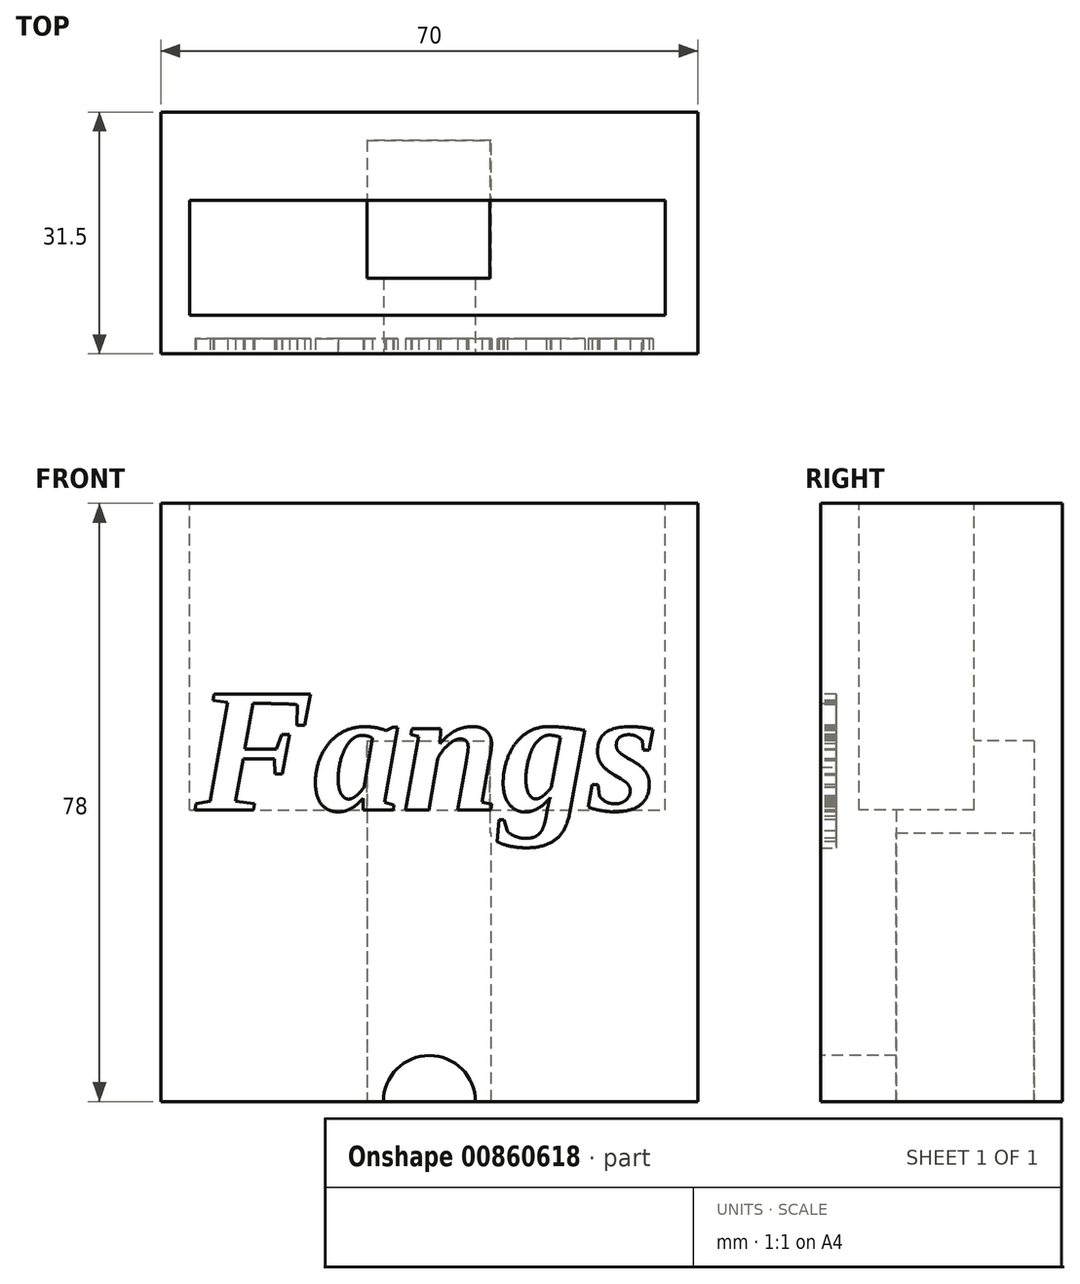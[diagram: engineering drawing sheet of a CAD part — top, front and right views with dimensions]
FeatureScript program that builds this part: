
annotation { "Feature Type Name" : "Feature", "Feature Type Description" : "" }
export const myFeature = defineFeature(function(context is Context, id is Id, definition is map)
    precondition{}
    {
        {
            var Q0;
            Q0=qCreatedBy(makeId("Front.planeOp"),FACE);
            var sketch = newSketch(context, id + "F0", { "sketchPlane" : qUnion([Q0])});
            skLineSegment(sketch, "E0", {"start": v(0, 0) * mm, "end": v(70, 0) * mm});
            skLineSegment(sketch, "E1", {"start": v(70, 0) * mm, "end": v(70, 40) * mm});
            skLineSegment(sketch, "E2", {"start": v(70, 40) * mm, "end": v(0, 40) * mm});
            skLineSegment(sketch, "E3", {"start": v(0, 40) * mm, "end": v(0, 0) * mm});
            skSolve(sketch);
        }
        {
            var Q0;
            Q0 = qSketchRegion(id + "F0", true);
            extrude(context, id + "F1", {"entities" : qUnion([Q0]), "depth" : 23 * mm, "offsetDistance" : 25 * mm});
        }
        {
            var Q0;
            Q0=makeQuery(id+"F1.opExtrude","CAP_FACE",FACE,{"disambiguationData":[OSD([sQuery(id+"F0.wireOp",EDGE,"E0"),sQuery(id+"F0.wireOp",EDGE,"E1"),sQuery(id+"F0.wireOp",EDGE,"E2"),sQuery(id+"F0.wireOp",EDGE,"E3")])],"isStart":false});
            var sketch = newSketch(context, id + "F2", { "sketchPlane" : qUnion([Q0])});
            skLineSegment(sketch, "E4.bottom", {"start": v(3.74, 0) * mm, "end": v(65.74, 0) * mm});
            skLineSegment(sketch, "E4.top", {"start": v(3.74, 40) * mm, "end": v(65.74, 40) * mm});
            skLineSegment(sketch, "E4.left", {"start": v(3.74, 0) * mm, "end": v(3.74, 40) * mm});
            skLineSegment(sketch, "E4.right", {"start": v(65.74, 0) * mm, "end": v(65.74, 40) * mm});
            skPoint(sketch, "E4.middle", {"position": v(34.74, 20) * mm});
            skSolve(sketch);
        }
        {
            var Q0;
            Q0 = qSketchRegion(id + "F2", true);
            extrude(context, id + "F3", {"entities" : qUnion([Q0]), "operationType" : NewBodyOperationType.REMOVE, "oppositeDirection" : true, "depth" : 15 * mm, "offsetDistance" : 25 * mm});
        }
        {
            var Q0;
            {var subQ0=sQuery(id+"F0.wireOp",EDGE,"E0");var subQ1=sQuery(id+"F0.wireOp",EDGE,"E3");var subQ2=sQuery(id+"F0.wireOp",EDGE,"E2");Q0=makeQuery(id+"F3.boolean.opBoolean","SPLIT",FACE,{"disambiguationData":[TD([makeQuery(id+"F1.opExtrude","SWEPT_FACE",FACE,{"disambiguationData":[OSD([subQ1])]})])],"derivedFrom":makeQuery(id+"F1.opExtrude","CAP_FACE",FACE,{"disambiguationData":[OSD([subQ0,sQuery(id+"F0.wireOp",EDGE,"E1"),subQ2,subQ1])],"isStart":false})});}
            var sketch = newSketch(context, id + "F4", { "sketchPlane" : qUnion([Q0])});
            skLineSegment(sketch, "E5.bottom", {"start": v(0, 0) * mm, "end": v(70, 0) * mm});
            skLineSegment(sketch, "E5.top", {"start": v(0, 40) * mm, "end": v(70, 40) * mm});
            skLineSegment(sketch, "E5.left", {"start": v(0, 0) * mm, "end": v(0, 40) * mm});
            skLineSegment(sketch, "E5.right", {"start": v(70, 0) * mm, "end": v(70, 40) * mm});
            skSolve(sketch);
        }
        {
            var Q0;
            Q0 = qSketchRegion(id + "F4", true);
            extrude(context, id + "F5", {"entities" : qUnion([Q0]), "operationType" : NewBodyOperationType.ADD, "depth" : 5 * mm, "offsetDistance" : 25 * mm});
        }
        {
            var Q0;
            Q0=makeQuery(id+"F5.boolean.opBoolean","MERGE",FACE,{"derivedFrom":[makeQuery(id+"F1.opExtrude","SWEPT_FACE",FACE,{"disambiguationData":[OSD([sQuery(id+"F0.wireOp",EDGE,"E0")])]}),makeQuery(id+"F5.opExtrude","SWEPT_FACE",FACE,{"disambiguationData":[OSD([sQuery(id+"F4.wireOp",EDGE,"E5.bottom")])]})]});
            var sketch = newSketch(context, id + "F6", { "sketchPlane" : qUnion([Q0])});
            skLineSegment(sketch, "E6.bottom", {"start": v(0, 0) * mm, "end": v(70, 0) * mm});
            skLineSegment(sketch, "E6.top", {"start": v(0, 28) * mm, "end": v(70, 28) * mm});
            skLineSegment(sketch, "E6.left", {"start": v(0, 0) * mm, "end": v(0, 28) * mm});
            skLineSegment(sketch, "E6.right", {"start": v(70, 0) * mm, "end": v(70, 28) * mm});
            skSolve(sketch);
        }
        {
            var Q0;
            Q0 = qSketchRegion(id + "F6", true);
            extrude(context, id + "F7", {"entities" : qUnion([Q0]), "operationType" : NewBodyOperationType.ADD, "depth" : 3 * mm, "offsetDistance" : 25 * mm});
        }
        {
            var Q0;
            Q0=makeQuery(id+"F7.opExtrude","CAP_FACE",FACE,{"disambiguationData":[OSD([sQuery(id+"F6.wireOp",EDGE,"E6.bottom"),sQuery(id+"F6.wireOp",EDGE,"E6.top"),sQuery(id+"F6.wireOp",EDGE,"E6.left"),sQuery(id+"F6.wireOp",EDGE,"E6.right")])],"isStart":false});
            var sketch = newSketch(context, id + "F8", { "sketchPlane" : qUnion([Q0])});
            skLineSegment(sketch, "E7.bottom", {"start": v(26.85, 0.17) * mm, "end": v(42.85, 0.17) * mm});
            skLineSegment(sketch, "E7.top", {"start": v(26.85, 18.17) * mm, "end": v(42.85, 18.17) * mm});
            skLineSegment(sketch, "E7.left", {"start": v(26.85, 0.17) * mm, "end": v(26.85, 18.17) * mm});
            skLineSegment(sketch, "E7.right", {"start": v(42.85, 0.17) * mm, "end": v(42.85, 18.17) * mm});
            skPoint(sketch, "E7.middle", {"position": v(34.85, 9.17) * mm});
            skSolve(sketch);
        }
        {
            var Q0;
            Q0 = qSketchRegion(id + "F8", true);
            extrude(context, id + "F9", {"entities" : qUnion([Q0]), "operationType" : NewBodyOperationType.REMOVE, "oppositeDirection" : true, "depth" : 12 * mm, "offsetDistance" : 25 * mm});
        }
        {
            var Q0;
            Q0=makeQuery(id+"F7.boolean.opBoolean","MERGE",FACE,{"derivedFrom":[makeQuery(id+"F1.opExtrude","CAP_FACE",FACE,{"disambiguationData":[OSD([sQuery(id+"F0.wireOp",EDGE,"E0"),sQuery(id+"F0.wireOp",EDGE,"E1"),sQuery(id+"F0.wireOp",EDGE,"E2"),sQuery(id+"F0.wireOp",EDGE,"E3")])],"isStart":true}),makeQuery(id+"F7.opExtrude","SWEPT_FACE",FACE,{"disambiguationData":[OSD([sQuery(id+"F6.wireOp",EDGE,"E6.bottom")])]})]});
            var sketch = newSketch(context, id + "F10", { "sketchPlane" : qUnion([Q0])});
            skLineSegment(sketch, "E8.bottom", {"start": v(0, -3) * mm, "end": v(-70, -3) * mm});
            skLineSegment(sketch, "E8.top", {"start": v(0, 40) * mm, "end": v(-70, 40) * mm});
            skLineSegment(sketch, "E8.left", {"start": v(0, -3) * mm, "end": v(0, 40) * mm});
            skLineSegment(sketch, "E8.right", {"start": v(-70, -3) * mm, "end": v(-70, 40) * mm});
            skSolve(sketch);
        }
        {
            var Q0;
            Q0 = qSketchRegion(id + "F10", true);
            extrude(context, id + "F11", {"entities" : qUnion([Q0]), "operationType" : NewBodyOperationType.ADD, "depth" : 3.5 * mm, "offsetDistance" : 25 * mm});
        }
        {
            var Q0;
            Q0=makeQuery(id+"F11.boolean.opBoolean","MERGE",FACE,{"derivedFrom":[makeQuery(id+"F7.opExtrude","CAP_FACE",FACE,{"disambiguationData":[OSD([sQuery(id+"F6.wireOp",EDGE,"E6.bottom"),sQuery(id+"F6.wireOp",EDGE,"E6.top"),sQuery(id+"F6.wireOp",EDGE,"E6.left"),sQuery(id+"F6.wireOp",EDGE,"E6.right")])],"isStart":false}),makeQuery(id+"F11.opExtrude","SWEPT_FACE",FACE,{"disambiguationData":[OSD([sQuery(id+"F10.wireOp",EDGE,"E8.bottom")])]})]});
            var sketch = newSketch(context, id + "F12", { "sketchPlane" : qUnion([Q0])});
            skLineSegment(sketch, "E9.bottom", {"start": v(0, -3.5) * mm, "end": v(26.85, -3.5) * mm});
            skLineSegment(sketch, "E9.top", {"start": v(0, 28) * mm, "end": v(26.85, 28) * mm});
            skLineSegment(sketch, "E9.left", {"start": v(0, -3.5) * mm, "end": v(0, 28) * mm});
            skLineSegment(sketch, "E9.right", {"start": v(26.85, -3.5) * mm, "end": v(26.85, 28) * mm});
            skLineSegment(sketch, "E10.bottom", {"start": v(26.85, 18.17) * mm, "end": v(43.05, 18.17) * mm});
            skLineSegment(sketch, "E10.top", {"start": v(26.85, 28) * mm, "end": v(43.05, 28) * mm});
            skLineSegment(sketch, "E10.left", {"start": v(26.85, 18.17) * mm, "end": v(26.85, 28) * mm});
            skLineSegment(sketch, "E10.right", {"start": v(43.05, 18.17) * mm, "end": v(43.05, 28) * mm});
            skLineSegment(sketch, "E11.bottom", {"start": v(43.05, 28) * mm, "end": v(70, 28) * mm});
            skLineSegment(sketch, "E11.top", {"start": v(43.05, -3.5) * mm, "end": v(70, -3.5) * mm});
            skLineSegment(sketch, "E11.left", {"start": v(43.05, 28) * mm, "end": v(43.05, -3.5) * mm});
            skLineSegment(sketch, "E11.right", {"start": v(70, 28) * mm, "end": v(70, -3.5) * mm});
            skLineSegment(sketch, "E12.bottom", {"start": v(43.05, -3.5) * mm, "end": v(26.85, -3.5) * mm});
            skLineSegment(sketch, "E12.top", {"start": v(43.05, 0.17) * mm, "end": v(26.85, 0.17) * mm});
            skLineSegment(sketch, "E12.left", {"start": v(43.05, -3.5) * mm, "end": v(43.05, 0.17) * mm});
            skLineSegment(sketch, "E12.right", {"start": v(26.85, -3.5) * mm, "end": v(26.85, 0.17) * mm});
            skSolve(sketch);
        }
        {
            var Q0;
            Q0 = qSketchRegion(id + "F12", true);
            extrude(context, id + "F13", {"entities" : qUnion([Q0]), "operationType" : NewBodyOperationType.ADD, "depth" : 35 * mm, "offsetDistance" : 25 * mm});
        }
        {
            var Q0;
            Q0=makeQuery(id+"F13.boolean.opBoolean","MERGE",FACE,{"derivedFrom":[makeQuery(id+"F7.boolean.opBoolean","MERGE",FACE,{"derivedFrom":[makeQuery(id+"F5.opExtrude","CAP_FACE",FACE,{"disambiguationData":[OSD([sQuery(id+"F4.wireOp",EDGE,"E5.bottom"),sQuery(id+"F4.wireOp",EDGE,"E5.top"),sQuery(id+"F4.wireOp",EDGE,"E5.left"),sQuery(id+"F4.wireOp",EDGE,"E5.right")])],"isStart":false}),makeQuery(id+"F7.opExtrude","SWEPT_FACE",FACE,{"disambiguationData":[OSD([sQuery(id+"F6.wireOp",EDGE,"E6.top")])]})]}),makeQuery(id+"F13.opExtrude","SWEPT_FACE",FACE,{"disambiguationData":[OSD([sQuery(id+"F12.wireOp",EDGE,"E9.top"),sQuery(id+"F12.wireOp",EDGE,"E10.top"),sQuery(id+"F12.wireOp",EDGE,"E11.bottom")])]})]});
            var sketch = newSketch(context, id + "F14", { "sketchPlane" : qUnion([Q0])});
            skText(sketch, "E13", { "text": "Fangs", "fontName": "Tinos-BoldItalic.ttf"});
            const initialGuessF14  = {"E13": [0.00446, 0, 1, 0, 0.01664]};
            skSetInitialGuess(sketch, initialGuessF14);
            skSolve(sketch);
        }
        {
            var Q0;
            Q0 = qSketchRegion(id + "F14", true);
            extrude(context, id + "F15", {"entities" : qUnion([Q0]), "operationType" : NewBodyOperationType.REMOVE, "oppositeDirection" : true, "depth" : 2 * mm, "offsetDistance" : 25 * mm});
        }
        {
            var Q0;
            {var subQ1=sQuery(id+"F12.wireOp",EDGE,"E11.bottom");var subQ2=sQuery(id+"F12.wireOp",EDGE,"E10.top");var subQ4=sQuery(id+"F12.wireOp",EDGE,"E9.top");var subQ5=sQuery(id+"F4.wireOp",EDGE,"E5.top");var subQ6=sQuery(id+"F4.wireOp",EDGE,"E5.left");var subQ7=sQuery(id+"F4.wireOp",EDGE,"E5.right");Q0=makeQuery(id+"F15.boolean.opBoolean","SPLIT",FACE,{"disambiguationData":[TD([makeQuery(id+"F1.opExtrude","SWEPT_FACE",FACE,{"disambiguationData":[OSD([sQuery(id+"F0.wireOp",EDGE,"E1")])]})])],"derivedFrom":makeQuery(id+"F13.boolean.opBoolean","MERGE",FACE,{"derivedFrom":[makeQuery(id+"F7.boolean.opBoolean","MERGE",FACE,{"derivedFrom":[makeQuery(id+"F5.opExtrude","CAP_FACE",FACE,{"disambiguationData":[OSD([sQuery(id+"F4.wireOp",EDGE,"E5.bottom"),subQ5,subQ6,subQ7])],"isStart":false}),makeQuery(id+"F7.opExtrude","SWEPT_FACE",FACE,{"disambiguationData":[OSD([sQuery(id+"F6.wireOp",EDGE,"E6.top")])]})]}),makeQuery(id+"F13.opExtrude","SWEPT_FACE",FACE,{"disambiguationData":[OSD([subQ4,subQ2,subQ1])]})]})});}
            var sketch = newSketch(context, id + "F16", { "sketchPlane" : qUnion([Q0])});
            skCircle(sketch, "E14", {"center": v(35, -38) * mm, "radius": 6 * mm});
            skSolve(sketch);
        }
        {
            var Q0;
            Q0 = qSketchRegion(id + "F16", true);
            extrude(context, id + "F17", {"entities" : qUnion([Q0]), "operationType" : NewBodyOperationType.REMOVE, "oppositeDirection" : true, "depth" : 15 * mm, "offsetDistance" : 25 * mm});
        }
    });
